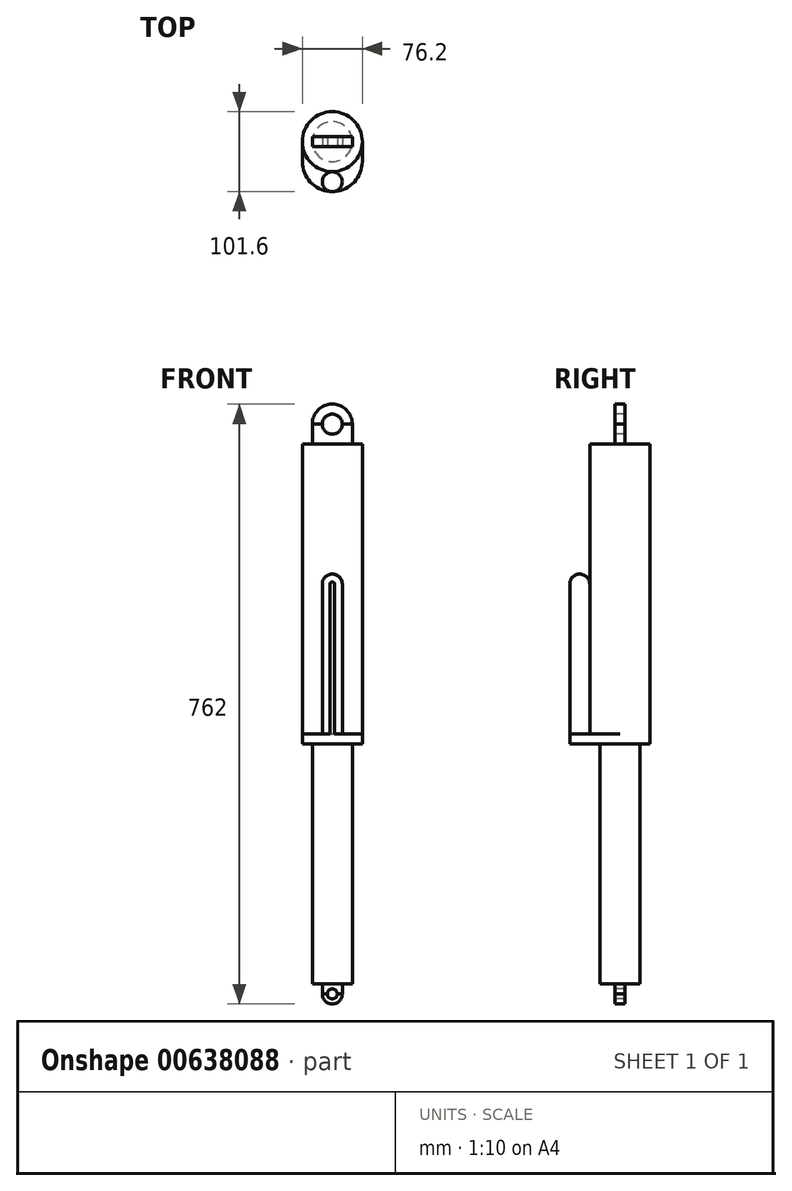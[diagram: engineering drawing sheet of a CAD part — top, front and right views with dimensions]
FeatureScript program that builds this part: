
annotation { "Feature Type Name" : "Feature", "Feature Type Description" : "" }
export const myFeature = defineFeature(function(context is Context, id is Id, definition is map)
    precondition{}
    {
        {
            var Q0;
            Q0=qCreatedBy(makeId("Top.planeOp"),FACE);
            var sketch = newSketch(context, id + "F0", { "sketchPlane" : qUnion([Q0])});
            skCircle(sketch, "E0", {"center": v(0, 0) * mm, "radius": 38.1 * mm});
            skSolve(sketch);
        }
        {
            var Q0;
            Q0=makeQuery(id+"F0.imprint","IMPRINT",FACE,{"disambiguationData":[TD([[makeQuery(id+"F0.imprint","IMPRINT",EDGE,{"derivedFrom":sQuery(id+"F0.wireOp",EDGE,"E0")}),1.0]])]});
            extrude(context, id + "F1", {"entities" : qUnion([Q0]), "depth" : 381 * mm, "offsetDistance" : 25.4 * mm});
        }
        {
            var Q0;
            Q0=qCreatedBy(makeId("Top.planeOp"),FACE);
            var sketch = newSketch(context, id + "F2", { "sketchPlane" : qUnion([Q0])});
            skCircle(sketch, "E1", {"center": v(0, 0) * mm, "radius": 25.4 * mm});
            skSolve(sketch);
        }
        {
            var Q0;
            Q0=makeQuery(id+"F2.imprint","IMPRINT",FACE,{"disambiguationData":[TD([[makeQuery(id+"F2.imprint","IMPRINT",EDGE,{"derivedFrom":sQuery(id+"F2.wireOp",EDGE,"E1")}),1.0]])]});
            extrude(context, id + "F3", {"entities" : qUnion([Q0]), "operationType" : NewBodyOperationType.ADD, "oppositeDirection" : true, "depth" : 304.8 * mm, "offsetDistance" : 25.4 * mm});
        }
        {
            var Q0;
            Q0=qCreatedBy(makeId("Top.planeOp"),FACE);
            var sketch = newSketch(context, id + "F4", { "sketchPlane" : qUnion([Q0])});
            skLineSegment(sketch, "E2.bottom", {"start": v(0, 0) * mm, "end": v(38.1, 0) * mm});
            skLineSegment(sketch, "E2.top", {"start": v(0, -63.5) * mm, "end": v(38.1, -63.5) * mm});
            skLineSegment(sketch, "E2.left", {"start": v(0, 0) * mm, "end": v(0, -63.5) * mm});
            skLineSegment(sketch, "E2.right", {"start": v(38.1, 0) * mm, "end": v(38.1, -63.5) * mm});
            skLineSegment(sketch, "E3.MirrorCS", {"start": v(0, 0) * mm, "end": v(-38.1, 0) * mm});
            skLineSegment(sketch, "E4.MirrorCS", {"start": v(-38.1, 0) * mm, "end": v(-38.1, -63.5) * mm});
            skLineSegment(sketch, "E5.MirrorCS", {"start": v(0, -63.5) * mm, "end": v(-38.1, -63.5) * mm});
            skSolve(sketch);
        }
        {
            var Q0;
            Q0=makeQuery(id+"F4.imprint","IMPRINT",FACE,{"disambiguationData":[TD([[makeQuery(id+"F4.imprint","IMPRINT",EDGE,{"derivedFrom":sQuery(id+"F4.wireOp",EDGE,"E2.bottom")}),-1.0]])]});
            var Q1;
            Q1=makeQuery(id+"F4.imprint","IMPRINT",FACE,{"disambiguationData":[TD([[makeQuery(id+"F4.imprint","IMPRINT",EDGE,{"derivedFrom":sQuery(id+"F4.wireOp",EDGE,"E2.left")}),-1.0]])]});
            extrude(context, id + "F5", {"entities" : qUnion([Q0, Q1]), "operationType" : NewBodyOperationType.ADD, "depth" : 12.7 * mm, "offsetDistance" : 25.4 * mm});
        }
        {
            var Q0;
            Q0=makeQuery(id+"F5.opExtrude","CAP_FACE",FACE,{"disambiguationData":[OSD([sQuery(id+"F4.wireOp",EDGE,"E2.bottom"),sQuery(id+"F4.wireOp",EDGE,"E2.top"),sQuery(id+"F4.wireOp",EDGE,"E2.right"),sQuery(id+"F4.wireOp",EDGE,"E3.MirrorCS"),sQuery(id+"F4.wireOp",EDGE,"E4.MirrorCS"),sQuery(id+"F4.wireOp",EDGE,"E5.MirrorCS")])],"isStart":false});
            var sketch = newSketch(context, id + "F6", { "sketchPlane" : qUnion([Q0])});
            skCircle(sketch, "E6", {"center": v(0, -51.06) * mm, "radius": 12.7 * mm});
            skSolve(sketch);
        }
        {
            var Q0;
            {var subQ0=sQuery(id+"F6.wireOp",EDGE,"E6");var subQ1=makeQuery(id+"F5.opExtrude","CAP_EDGE",EDGE,{"disambiguationData":[OSD([sQuery(id+"F4.wireOp",EDGE,"E2.top"),sQuery(id+"F4.wireOp",EDGE,"E5.MirrorCS")])],"isStart":false});var subQ2=makeQuery(id+"F6.imprint","INTERSECT",VERTEX,{"disambiguationData":[OD(0.0)],"derivedFrom":[subQ1,subQ0]});Q0=makeQuery(id+"F6.imprint","IMPRINT",FACE,{"disambiguationData":[TD([[makeQuery(id+"F6.imprint","IMPRINT",EDGE,{"disambiguationData":[TD([[subQ2,-1.0]])],"derivedFrom":subQ0}),1.0]])]});}
            extrude(context, id + "F7", {"entities" : qUnion([Q0]), "operationType" : NewBodyOperationType.ADD, "depth" : 203.2 * mm, "offsetDistance" : 25.4 * mm});
        }
        {
            var Q0;
            Q0=makeQuery(id+"F1.opExtrude","CAP_FACE",FACE,{"disambiguationData":[OSD([sQuery(id+"F0.wireOp",EDGE,"E0")])],"isStart":false});
            var sketch = newSketch(context, id + "F8", { "sketchPlane" : qUnion([Q0])});
            skLineSegment(sketch, "E7.bottom", {"start": v(25.4, -6.35) * mm, "end": v(-25.4, -6.35) * mm});
            skLineSegment(sketch, "E7.top", {"start": v(25.4, 6.35) * mm, "end": v(-25.4, 6.35) * mm});
            skLineSegment(sketch, "E7.left", {"start": v(25.4, -6.35) * mm, "end": v(25.4, 6.35) * mm});
            skLineSegment(sketch, "E7.right", {"start": v(-25.4, -6.35) * mm, "end": v(-25.4, 6.35) * mm});
            skPoint(sketch, "E7.middle", {"position": v(0, 0) * mm});
            skSolve(sketch);
        }
        {
            var Q0;
            Q0=makeQuery(id+"F8.imprint","IMPRINT",FACE,{"disambiguationData":[TD([[makeQuery(id+"F8.imprint","IMPRINT",EDGE,{"derivedFrom":sQuery(id+"F8.wireOp",EDGE,"E7.bottom")}),-1.0]])]});
            extrude(context, id + "F9", {"entities" : qUnion([Q0]), "operationType" : NewBodyOperationType.ADD, "depth" : 25.4 * mm, "offsetDistance" : 25.4 * mm});
        }
        {
            var Q0;
            Q0=makeQuery(id+"F9.opExtrude","SWEPT_FACE",FACE,{"disambiguationData":[OSD([sQuery(id+"F8.wireOp",EDGE,"E7.bottom")])]});
            var sketch = newSketch(context, id + "F10", { "sketchPlane" : qUnion([Q0])});
            skArc(sketch, "E8", {"start": v(25.4, 406.4) * mm, "mid": v(0, 431.8) * mm, "end": v(-25.4, 406.4) * mm});
            skSolve(sketch);
        }
        {
            var Q0;
            Q0=makeQuery(id+"F10.imprint","IMPRINT",FACE,{"disambiguationData":[TD([[makeQuery(id+"F10.imprint","IMPRINT",EDGE,{"derivedFrom":sQuery(id+"F10.wireOp",EDGE,"E8")}),1.0]])]});
            extrude(context, id + "F11", {"entities" : qUnion([Q0]), "oppositeDirection" : true, "depth" : 12.7 * mm, "offsetDistance" : 25.4 * mm});
        }
        {
            var Q0;
            Q0=makeQuery(id+"F11.opExtrude","CAP_FACE",FACE,{"disambiguationData":[OSD([sQuery(id+"F8.wireOp",EDGE,"E7.bottom"),sQuery(id+"F10.wireOp",EDGE,"E8")])],"isStart":true});
            var sketch = newSketch(context, id + "F12", { "sketchPlane" : qUnion([Q0])});
            skPoint(sketch, "E9", {"position": v(0, 406.4) * mm});
            skSolve(sketch);
        }
        {
            var Q0;
            Q0=sQuery(id+"F12.wireOp",VERTEX,"E9");
            var Q1;
            Q1=makeQuery(id+"F1.opExtrude","SWEPT_BODY",BODY,{"disambiguationData":[OSD([sQuery(id+"F0.wireOp",EDGE,"E0")])]});
            var Q2;
            Q2=makeQuery(id+"F11.opExtrude","SWEPT_BODY",BODY,{"disambiguationData":[OSD([sQuery(id+"F8.wireOp",EDGE,"E7.bottom"),sQuery(id+"F10.wireOp",EDGE,"E8")])]});
            hole(context, id + "F13", {"style" : HoleStyle.SIMPLE, "endStyle" : HoleEndStyle.THROUGH, "holeDiameter" : 25.4 * mm, "majorDiameter" : 6.35 * mm, "isTappedThrough" : true, "tappedDepth" : 12.7 * mm, "tapClearance" : 3, "locations" : qUnion([Q0]), "scope" : qUnion([Q1, Q2])});
        }
        {
            var Q0;
            Q0=makeQuery(id+"F3.opExtrude","CAP_FACE",FACE,{"disambiguationData":[OSD([sQuery(id+"F2.wireOp",EDGE,"E1")])],"isStart":false});
            var sketch = newSketch(context, id + "F14", { "sketchPlane" : qUnion([Q0])});
            skLineSegment(sketch, "E10.bottom", {"start": v(12.7, -6.35) * mm, "end": v(-12.7, -6.35) * mm});
            skLineSegment(sketch, "E10.top", {"start": v(12.7, 6.35) * mm, "end": v(-12.7, 6.35) * mm});
            skLineSegment(sketch, "E10.left", {"start": v(12.7, -6.35) * mm, "end": v(12.7, 6.35) * mm});
            skLineSegment(sketch, "E10.right", {"start": v(-12.7, -6.35) * mm, "end": v(-12.7, 6.35) * mm});
            skPoint(sketch, "E10.middle", {"position": v(0, 0) * mm});
            skSolve(sketch);
        }
        {
            var Q0;
            Q0=makeQuery(id+"F14.imprint","IMPRINT",FACE,{"disambiguationData":[TD([[makeQuery(id+"F14.imprint","IMPRINT",EDGE,{"derivedFrom":sQuery(id+"F14.wireOp",EDGE,"E10.bottom")}),-1.0]])]});
            extrude(context, id + "F15", {"entities" : qUnion([Q0]), "operationType" : NewBodyOperationType.ADD, "depth" : 12.7 * mm, "offsetDistance" : 25.4 * mm});
        }
        {
            var Q0;
            Q0=makeQuery(id+"F15.opExtrude","SWEPT_FACE",FACE,{"disambiguationData":[OSD([sQuery(id+"F14.wireOp",EDGE,"E10.top")])]});
            var sketch = newSketch(context, id + "F16", { "sketchPlane" : qUnion([Q0])});
            skArc(sketch, "E11", {"start": v(-12.7, -317.5) * mm, "mid": v(0, -330.2) * mm, "end": v(12.7, -317.5) * mm});
            skSolve(sketch);
        }
        {
            var Q0;
            Q0=makeQuery(id+"F16.imprint","IMPRINT",FACE,{"disambiguationData":[TD([[makeQuery(id+"F16.imprint","IMPRINT",EDGE,{"derivedFrom":sQuery(id+"F16.wireOp",EDGE,"E11")}),1.0]])]});
            extrude(context, id + "F17", {"entities" : qUnion([Q0]), "oppositeDirection" : true, "depth" : 12.7 * mm, "offsetDistance" : 25.4 * mm});
        }
        {
            var Q0;
            Q0=makeQuery(id+"F17.opExtrude","CAP_FACE",FACE,{"disambiguationData":[OSD([sQuery(id+"F14.wireOp",EDGE,"E10.top"),sQuery(id+"F16.wireOp",EDGE,"E11")])],"isStart":true});
            var sketch = newSketch(context, id + "F18", { "sketchPlane" : qUnion([Q0])});
            skPoint(sketch, "E12", {"position": v(0, -317.5) * mm});
            skSolve(sketch);
        }
        {
            var Q0;
            Q0=sQuery(id+"F18.wireOp",VERTEX,"E12");
            var Q1;
            Q1=makeQuery(id+"F1.opExtrude","SWEPT_BODY",BODY,{"disambiguationData":[OSD([sQuery(id+"F0.wireOp",EDGE,"E0")])]});
            var Q2;
            Q2=makeQuery(id+"F17.opExtrude","SWEPT_BODY",BODY,{"disambiguationData":[OSD([sQuery(id+"F14.wireOp",EDGE,"E10.top"),sQuery(id+"F16.wireOp",EDGE,"E11")])]});
            hole(context, id + "F19", {"style" : HoleStyle.SIMPLE, "endStyle" : HoleEndStyle.THROUGH, "holeDiameter" : 12.7 * mm, "majorDiameter" : 6.35 * mm, "isTappedThrough" : true, "tappedDepth" : 12.7 * mm, "tapClearance" : 3, "locations" : qUnion([Q0]), "scope" : qUnion([Q1, Q2])});
        }
        {
            var Q0;
            Q0=makeQuery(id+"F5.opExtrude","SWEPT_EDGE",EDGE,{"disambiguationData":[OSD([sQuery(id+"F4.wireOp",EDGE,"E4.MirrorCS"),sQuery(id+"F4.wireOp",EDGE,"E5.MirrorCS")])]});
            var Q1;
            Q1=makeQuery(id+"F5.opExtrude","SWEPT_EDGE",EDGE,{"disambiguationData":[OSD([sQuery(id+"F4.wireOp",EDGE,"E2.top"),sQuery(id+"F4.wireOp",EDGE,"E2.right")])]});
            fillet(context, id + "F20", {"entities" : qUnion([Q0, Q1]), "radius" : 38.1 * mm, "tangentPropagation" : true, "allowEdgeOverflow" : false});
        }
        {
            var Q0;
            Q0=makeQuery(id+"F7.opExtrude","CAP_EDGE",EDGE,{"disambiguationData":[OSD([sQuery(id+"F6.wireOp",EDGE,"E6")])],"isStart":false});
            fillet(context, id + "F21", {"entities" : qUnion([Q0]), "radius" : 12.7 * mm, "tangentPropagation" : true, "allowEdgeOverflow" : false});
        }
    });
